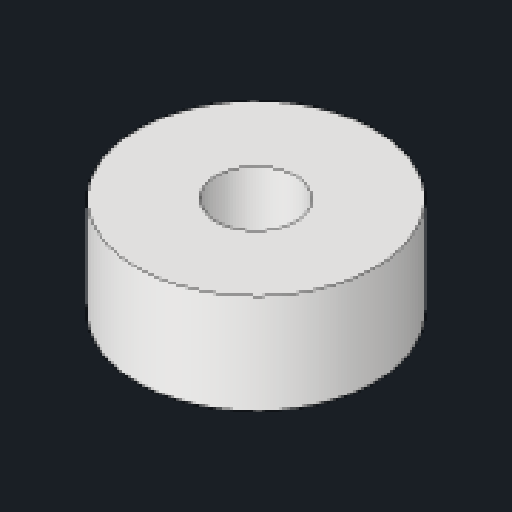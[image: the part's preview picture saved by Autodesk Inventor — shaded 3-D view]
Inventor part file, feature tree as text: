
AUTODESK INVENTOR PART (.ipt)
format: ipt  version: 2023.2 (Build 272271030, 271C)  size: 88,576 bytes
history: native  units: mm
features: revolve x1, sketch x1
ambient origin geometry x8: Origin, YZ Plane, XZ Plane, XY Plane, X Axis, Y Axis, Z Axis, Center Point
bodies: Solid1 (feature_tree)
feature tree (2):
  revolve  "Revolution1"  [1 undecoded]
  sketch  "Sketch1"  dims[d0=3.0mm d1=1.0mm d2=2.5mm d3=90.0deg]
note: 1 required parameter value undecoded (feature->parameter linkage not recoverable at this tier; creation-order binding heuristic only, values carry confidence <= 0.55)
